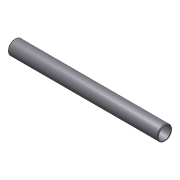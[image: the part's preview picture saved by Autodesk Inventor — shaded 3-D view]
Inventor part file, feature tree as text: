
AUTODESK INVENTOR PART (.ipt)
format: ipt  version: 2012 (Build 160160000, 160)  size: 111,104 bytes
history: native  units: in
note: dims shown in document units (in); Inventor stores cm internally (conversion verified against a paired STEP export)
features: other x42, revolve x1, sketch x1
ambient origin geometry x8: Origin, YZ Plane, XZ Plane, XY Plane, X Axis, Y Axis, Z Axis, Center Point
bodies: Solid1 (feature_tree)
feature tree (44):
  revolve  "Revolution1"  [1 undecoded]
  other  "tube_front_XY"
  other  "tube_front_YZ"
  other  "tube_front_ZX"
  other  "tube_front_X"
  other  "tube_front_Y"
  other  "tube_front_Z"
  other  "tube_front_Center"
  other  "tube_rear_XY"
  other  "tube_rear_YZ"
  other  "tube_rear_ZX"
  other  "tube_rear_X"
  other  "tube_rear_Y"
  other  "tube_rear_Z"
  other  "tube_rear_Center"
  other  "cp1_XY"
  other  "cp1_YZ"
  other  "cp1_ZX"
  other  "cp1_X"
  other  "cp1_Y"
  other  "cp1_Z"
  other  "cp1_Center"
  other  "cp2_XY"
  other  "cp2_YZ"
  other  "cp2_ZX"
  other  "cp2_X"
  other  "cp2_Y"
  other  "cp2_Z"
  other  "cp2_Center"
  other  "cp3_XY"
  other  "cp3_YZ"
  other  "cp3_ZX"
  other  "cp3_X"
  other  "cp3_Y"
  other  "cp3_Z"
  other  "cp3_Center"
  other  "cp4_XY"
  other  "cp4_YZ"
  other  "cp4_ZX"
  other  "cp4_X"
  other  "cp4_Y"
  other  "cp4_Z"
  other  "cp4_Center"
  sketch  "Sketch_1"  dims[d0=360.0deg]
note: 1 required parameter value undecoded (feature->parameter linkage not recoverable at this tier; creation-order binding heuristic only, values carry confidence <= 0.55)
